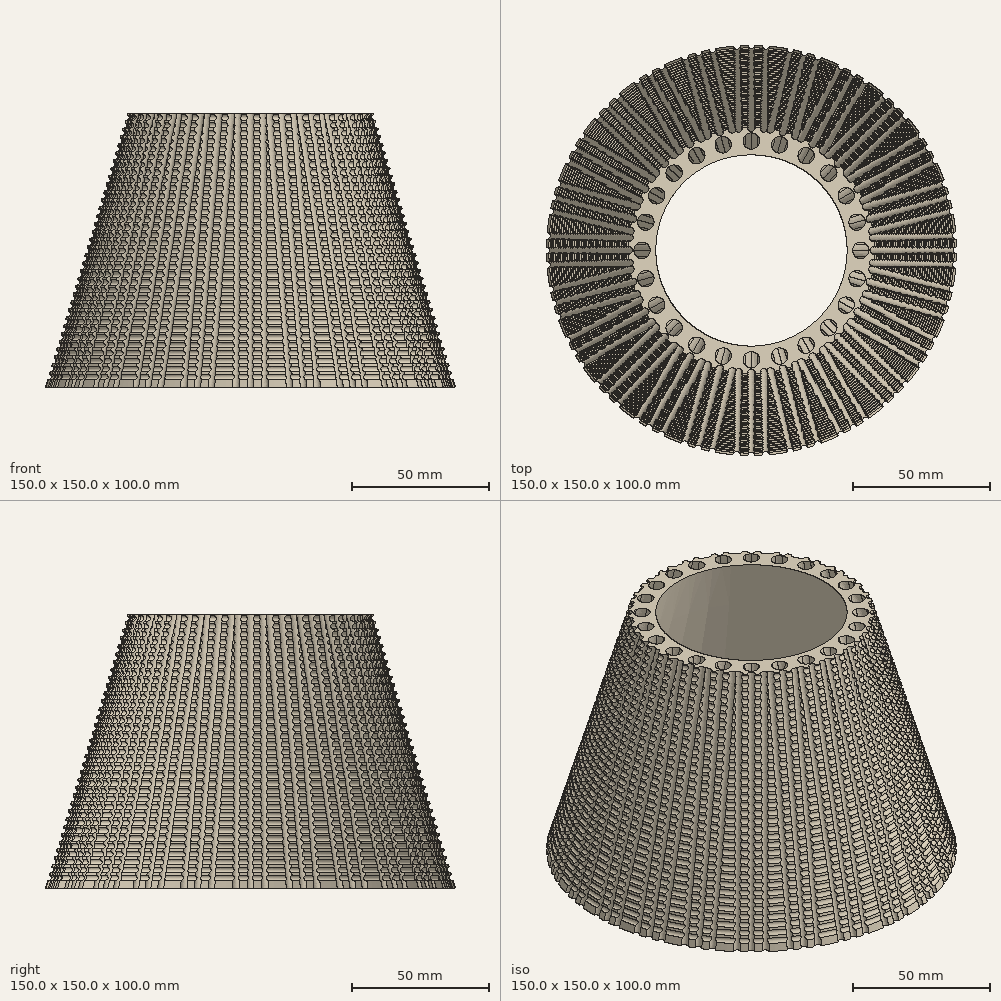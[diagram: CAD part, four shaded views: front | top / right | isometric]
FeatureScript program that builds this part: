
annotation { "Feature Type Name" : "Feature", "Feature Type Description" : "" }
export const myFeature = defineFeature(function(context is Context, id is Id, definition is map)
    precondition{}
    {
        {
            var Q0;
            Q0=qCreatedBy(makeId("Top.planeOp"),FACE);
            var sketch = newSketch(context, id + "F0", { "sketchPlane" : qUnion([Q0])});
            skCircle(sketch, "E0", {"center": v(0, 0) * mm, "radius": 75 * mm, "construction": true});
            skCircle(sketch, "E1", {"center": v(0, 0) * mm, "radius": 65 * mm, "construction": true});
            skLineSegment(sketch, "E2", {"start": v(-65, 0) * mm, "end": v(-75, 0) * mm, "construction": true});
            skCircle(sketch, "E3", {"center": v(-70, 0) * mm, "radius": 1 * mm});
            skCircle(sketch, "E4", {"center": v(-75, 0) * mm, "radius": 1.25 * mm});
            skLineSegment(sketch, "E5", {"start": v(0, 0) * mm, "end": v(-74.95, 2.62) * mm, "construction": true});
            skCircle(sketch, "E6", {"center": v(0, 0) * mm, "radius": 67.5 * mm, "construction": true});
            skCircle(sketch, "E7", {"center": v(0, 0) * mm, "radius": 72.5 * mm, "construction": true});
            skCircle(sketch, "E8", {"center": v(-72.46, 2.53) * mm, "radius": 1 * mm});
            skCircle(sketch, "E9", {"center": v(-67.46, 2.36) * mm, "radius": 1 * mm});
            skCircle(sketch, "E10", {"center": v(0, 0) * mm, "radius": 70 * mm, "construction": true});
            skLineSegment(sketch, "E11", {"start": v(0, 0) * mm, "end": v(-74.95, -2.62) * mm, "construction": true});
            skCircle(sketch, "E12", {"center": v(-67.46, -2.36) * mm, "radius": 1 * mm});
            skCircle(sketch, "E13", {"center": v(-72.46, -2.53) * mm, "radius": 1 * mm});
            skLineSegment(sketch, "E14", {"start": v(0, 0) * mm, "end": v(-74.82, -5.23) * mm, "construction": true});
            skLineSegment(sketch, "E15", {"start": v(0, 0) * mm, "end": v(-74.82, 5.23) * mm, "construction": true});
            skCircle(sketch, "E16", {"center": v(-74.82, -5.23) * mm, "radius": 1.25 * mm});
            skCircle(sketch, "E17", {"center": v(-74.82, 5.23) * mm, "radius": 1.25 * mm});
            skCircle(sketch, "E18", {"center": v(-69.83, -4.88) * mm, "radius": 1 * mm});
            skCircle(sketch, "E19", {"center": v(-69.83, 4.88) * mm, "radius": 1 * mm});
            skSolve(sketch);
        }
        {
            var Q0;
            Q0=qCreatedBy(makeId("Top.planeOp"),FACE);
            var sketch = newSketch(context, id + "F1", { "sketchPlane" : qUnion([Q0])});
            skCircle(sketch, "E20.0", {"center": v(0, 0) * mm, "radius": 75 * mm});
            skSolve(sketch);
        }
        {
            var Q0;
            Q0=qCreatedBy(makeId("Top.planeOp"),FACE);
            var sketch = newSketch(context, id + "F2", { "sketchPlane" : qUnion([Q0])});
            skCircle(sketch, "E21.0", {"center": v(0, 0) * mm, "radius": 65 * mm});
            skSolve(sketch);
        }
        {
            var Q0;
            Q0=qCreatedBy(makeId("Top.planeOp"),FACE);
            cPlane(context, id + "F3", {"entities" : qUnion([Q0]), "cplaneType" : CPlaneType.OFFSET, "offset" : 100 * mm, "width" : 150 * mm, "height" : 150 * mm});
        }
        {
            var Q0;
            Q0=qCreatedBy(id+"F3.planeOp",FACE);
            var sketch = newSketch(context, id + "F4", { "sketchPlane" : qUnion([Q0])});
            skCircle(sketch, "E22", {"center": v(0, 0) * mm, "radius": 35 * mm, "construction": true});
            skCircle(sketch, "E23", {"center": v(0, 0) * mm, "radius": 45 * mm, "construction": true});
            skLineSegment(sketch, "E24", {"start": v(-35, 0) * mm, "end": v(-45, 0) * mm, "construction": true});
            skCircle(sketch, "E25", {"center": v(0, 0) * mm, "radius": 37.5 * mm, "construction": true});
            skCircle(sketch, "E26", {"center": v(0, 0) * mm, "radius": 42.5 * mm, "construction": true});
            skCircle(sketch, "E27", {"center": v(-40, 0) * mm, "radius": 3 * mm});
            skCircle(sketch, "E28", {"center": v(-45, 0) * mm, "radius": 1.5 * mm});
            skLineSegment(sketch, "E29", {"start": v(0, 0) * mm, "end": v(-44.75, -4.7) * mm, "construction": true});
            skLineSegment(sketch, "E30", {"start": v(0, 0) * mm, "end": v(-44.75, 4.7) * mm, "construction": true});
            skCircle(sketch, "E31", {"center": v(-44.75, -4.7) * mm, "radius": 1.5 * mm});
            skCircle(sketch, "E32", {"center": v(-44.75, 4.7) * mm, "radius": 1.5 * mm});
            skSolve(sketch);
        }
        {
            var Q0;
            Q0=qCreatedBy(id+"F3.planeOp",FACE);
            var sketch = newSketch(context, id + "F5", { "sketchPlane" : qUnion([Q0])});
            skCircle(sketch, "E33.0", {"center": v(0, 0) * mm, "radius": 35 * mm});
            skSolve(sketch);
        }
        {
            var Q0;
            Q0=qCreatedBy(id+"F3.planeOp",FACE);
            var sketch = newSketch(context, id + "F6", { "sketchPlane" : qUnion([Q0])});
            skCircle(sketch, "E34.0", {"center": v(0, 0) * mm, "radius": 45 * mm});
            skSolve(sketch);
        }
        {
            var Q0;
            Q0=makeQuery(id+"F4.imprint","IMPRINT",FACE,{"disambiguationData":[TD([[makeQuery(id+"F4.imprint","IMPRINT",EDGE,{"derivedFrom":sQuery(id+"F4.wireOp",EDGE,"E28")}),1.0]])]});
            var Q1;
            Q1=makeQuery(id+"F0.imprint","IMPRINT",FACE,{"disambiguationData":[TD([[makeQuery(id+"F0.imprint","IMPRINT",EDGE,{"derivedFrom":sQuery(id+"F0.wireOp",EDGE,"E4")}),1.0]])]});
            loft(context, id + "F7", {"sheetProfilesArray" : [{ "sheetProfileEntities" : qUnion([Q0]) }, { "sheetProfileEntities" : qUnion([Q1]) }]});
        }
        {
            var Q1;
            Q1=makeQuery(id+"F4.imprint","IMPRINT",FACE,{"disambiguationData":[TD([[makeQuery(id+"F4.imprint","IMPRINT",EDGE,{"derivedFrom":sQuery(id+"F4.wireOp",EDGE,"E27")}),1.0]])]});
            var Q2;
            Q2=makeQuery(id+"F0.imprint","IMPRINT",FACE,{"disambiguationData":[TD([[makeQuery(id+"F0.imprint","IMPRINT",EDGE,{"derivedFrom":sQuery(id+"F0.wireOp",EDGE,"E8")}),1.0]])]});
            loft(context, id + "F8", {"operationType" : NewBodyOperationType.ADD, "sheetProfilesArray" : [{ "sheetProfileEntities" : qUnion([Q1]) }, { "sheetProfileEntities" : qUnion([Q2]) }]});
        }
        {
            var Q1;
            Q1=makeQuery(id+"F4.imprint","IMPRINT",FACE,{"disambiguationData":[TD([[makeQuery(id+"F4.imprint","IMPRINT",EDGE,{"derivedFrom":sQuery(id+"F4.wireOp",EDGE,"E27")}),1.0]])]});
            var Q2;
            Q2=makeQuery(id+"F0.imprint","IMPRINT",FACE,{"disambiguationData":[TD([[makeQuery(id+"F0.imprint","IMPRINT",EDGE,{"derivedFrom":sQuery(id+"F0.wireOp",EDGE,"E9")}),1.0]])]});
            loft(context, id + "F9", {"operationType" : NewBodyOperationType.ADD, "sheetProfilesArray" : [{ "sheetProfileEntities" : qUnion([Q1]) }, { "sheetProfileEntities" : qUnion([Q2]) }]});
        }
        {
            var Q1;
            Q1=makeQuery(id+"F4.imprint","IMPRINT",FACE,{"disambiguationData":[TD([[makeQuery(id+"F4.imprint","IMPRINT",EDGE,{"derivedFrom":sQuery(id+"F4.wireOp",EDGE,"E27")}),1.0]])]});
            var Q2;
            Q2=makeQuery(id+"F0.imprint","IMPRINT",FACE,{"disambiguationData":[TD([[makeQuery(id+"F0.imprint","IMPRINT",EDGE,{"derivedFrom":sQuery(id+"F0.wireOp",EDGE,"E19")}),1.0]])]});
            loft(context, id + "F10", {"operationType" : NewBodyOperationType.ADD, "sheetProfilesArray" : [{ "sheetProfileEntities" : qUnion([Q1]) }, { "sheetProfileEntities" : qUnion([Q2]) }]});
        }
        {
            var Q1;
            Q1=makeQuery(id+"F4.imprint","IMPRINT",FACE,{"disambiguationData":[TD([[makeQuery(id+"F4.imprint","IMPRINT",EDGE,{"derivedFrom":sQuery(id+"F4.wireOp",EDGE,"E27")}),1.0]])]});
            var Q2;
            Q2=makeQuery(id+"F0.imprint","IMPRINT",FACE,{"disambiguationData":[TD([[makeQuery(id+"F0.imprint","IMPRINT",EDGE,{"derivedFrom":sQuery(id+"F0.wireOp",EDGE,"E3")}),1.0]])]});
            loft(context, id + "F11", {"operationType" : NewBodyOperationType.ADD, "sheetProfilesArray" : [{ "sheetProfileEntities" : qUnion([Q1]) }, { "sheetProfileEntities" : qUnion([Q2]) }]});
        }
        {
            var Q1;
            Q1=makeQuery(id+"F4.imprint","IMPRINT",FACE,{"disambiguationData":[TD([[makeQuery(id+"F4.imprint","IMPRINT",EDGE,{"derivedFrom":sQuery(id+"F4.wireOp",EDGE,"E27")}),1.0]])]});
            var Q2;
            Q2=makeQuery(id+"F0.imprint","IMPRINT",FACE,{"disambiguationData":[TD([[makeQuery(id+"F0.imprint","IMPRINT",EDGE,{"derivedFrom":sQuery(id+"F0.wireOp",EDGE,"E12")}),1.0]])]});
            loft(context, id + "F12", {"operationType" : NewBodyOperationType.ADD, "sheetProfilesArray" : [{ "sheetProfileEntities" : qUnion([Q1]) }, { "sheetProfileEntities" : qUnion([Q2]) }]});
        }
        {
            var Q1;
            Q1=makeQuery(id+"F4.imprint","IMPRINT",FACE,{"disambiguationData":[TD([[makeQuery(id+"F4.imprint","IMPRINT",EDGE,{"derivedFrom":sQuery(id+"F4.wireOp",EDGE,"E27")}),1.0]])]});
            var Q2;
            Q2=makeQuery(id+"F0.imprint","IMPRINT",FACE,{"disambiguationData":[TD([[makeQuery(id+"F0.imprint","IMPRINT",EDGE,{"derivedFrom":sQuery(id+"F0.wireOp",EDGE,"E13")}),1.0]])]});
            loft(context, id + "F13", {"operationType" : NewBodyOperationType.ADD, "sheetProfilesArray" : [{ "sheetProfileEntities" : qUnion([Q1]) }, { "sheetProfileEntities" : qUnion([Q2]) }]});
        }
        {
            var Q1;
            Q1=makeQuery(id+"F4.imprint","IMPRINT",FACE,{"disambiguationData":[TD([[makeQuery(id+"F4.imprint","IMPRINT",EDGE,{"derivedFrom":sQuery(id+"F4.wireOp",EDGE,"E27")}),1.0]])]});
            var Q2;
            Q2=makeQuery(id+"F0.imprint","IMPRINT",FACE,{"disambiguationData":[TD([[makeQuery(id+"F0.imprint","IMPRINT",EDGE,{"derivedFrom":sQuery(id+"F0.wireOp",EDGE,"E18")}),1.0]])]});
            loft(context, id + "F14", {"operationType" : NewBodyOperationType.ADD, "sheetProfilesArray" : [{ "sheetProfileEntities" : qUnion([Q1]) }, { "sheetProfileEntities" : qUnion([Q2]) }]});
        }
        {
            var Q0;
            Q0=makeQuery(id+"F4.imprint","IMPRINT",FACE,{"disambiguationData":[TD([[makeQuery(id+"F4.imprint","IMPRINT",EDGE,{"derivedFrom":sQuery(id+"F4.wireOp",EDGE,"E32")}),1.0]])]});
            var Q1;
            Q1=makeQuery(id+"F0.imprint","IMPRINT",FACE,{"disambiguationData":[TD([[makeQuery(id+"F0.imprint","IMPRINT",EDGE,{"derivedFrom":sQuery(id+"F0.wireOp",EDGE,"E17")}),1.0]])]});
            loft(context, id + "F15", {"sheetProfilesArray" : [{ "sheetProfileEntities" : qUnion([Q0]) }, { "sheetProfileEntities" : qUnion([Q1]) }]});
        }
        {
            var Q0;
            Q0=makeQuery(id+"F4.imprint","IMPRINT",FACE,{"disambiguationData":[TD([[makeQuery(id+"F4.imprint","IMPRINT",EDGE,{"derivedFrom":sQuery(id+"F4.wireOp",EDGE,"E31")}),1.0]])]});
            var Q1;
            Q1=makeQuery(id+"F0.imprint","IMPRINT",FACE,{"disambiguationData":[TD([[makeQuery(id+"F0.imprint","IMPRINT",EDGE,{"derivedFrom":sQuery(id+"F0.wireOp",EDGE,"E16")}),1.0]])]});
            loft(context, id + "F16", {"sheetProfilesArray" : [{ "sheetProfileEntities" : qUnion([Q0]) }, { "sheetProfileEntities" : qUnion([Q1]) }]});
        }
        {
            var Q0;
            Q0=makeQuery(id+"F1.imprint","IMPRINT",FACE,{"disambiguationData":[TD([[makeQuery(id+"F1.imprint","IMPRINT",EDGE,{"derivedFrom":sQuery(id+"F1.wireOp",EDGE,"E20.0")}),1.0]])]});
            var Q1;
            Q1=makeQuery(id+"F6.imprint","IMPRINT",FACE,{"disambiguationData":[TD([[makeQuery(id+"F6.imprint","IMPRINT",EDGE,{"derivedFrom":sQuery(id+"F6.wireOp",EDGE,"E34.0")}),1.0]])]});
            loft(context, id + "F17", {"sheetProfilesArray" : [{ "sheetProfileEntities" : qUnion([Q0]) }, { "sheetProfileEntities" : qUnion([Q1]) }]});
        }
        {
            var Q1;
            Q1=makeQuery(id+"F2.imprint","IMPRINT",FACE,{"disambiguationData":[TD([[makeQuery(id+"F2.imprint","IMPRINT",EDGE,{"derivedFrom":sQuery(id+"F2.wireOp",EDGE,"E21.0")}),1.0]])]});
            var Q2;
            Q2=makeQuery(id+"F5.imprint","IMPRINT",FACE,{"disambiguationData":[TD([[makeQuery(id+"F5.imprint","IMPRINT",EDGE,{"derivedFrom":sQuery(id+"F5.wireOp",EDGE,"E33.0")}),1.0]])]});
            loft(context, id + "F18", {"operationType" : NewBodyOperationType.REMOVE, "sheetProfilesArray" : [{ "sheetProfileEntities" : qUnion([Q1]) }, { "sheetProfileEntities" : qUnion([Q2]) }]});
        }
        {
            var Q0;
            Q0=makeQuery(id+"F7.opLoft","SWEPT_BODY",BODY,{"disambiguationData":[OSD([makeQuery(id+"F0.imprint","IMPRINT",FACE,{"disambiguationData":[TD([[makeQuery(id+"F0.imprint","IMPRINT",EDGE,{"derivedFrom":sQuery(id+"F0.wireOp",EDGE,"E4")}),1.0]])]}),makeQuery(id+"F4.imprint","IMPRINT",FACE,{"disambiguationData":[TD([[makeQuery(id+"F4.imprint","IMPRINT",EDGE,{"derivedFrom":sQuery(id+"F4.wireOp",EDGE,"E28")}),1.0]])]})])]});
            var Q1;
            Q1=makeQuery(id+"F8.opLoft","SWEPT_BODY",BODY,{"disambiguationData":[OSD([makeQuery(id+"F0.imprint","IMPRINT",FACE,{"disambiguationData":[TD([[makeQuery(id+"F0.imprint","IMPRINT",EDGE,{"derivedFrom":sQuery(id+"F0.wireOp",EDGE,"E8")}),1.0]])]}),makeQuery(id+"F4.imprint","IMPRINT",FACE,{"disambiguationData":[TD([[makeQuery(id+"F4.imprint","IMPRINT",EDGE,{"derivedFrom":sQuery(id+"F4.wireOp",EDGE,"E27")}),1.0]])]})])]});
            var Q2;
            Q2=makeQuery(id+"F15.opLoft","SWEPT_BODY",BODY,{"disambiguationData":[OSD([makeQuery(id+"F0.imprint","IMPRINT",FACE,{"disambiguationData":[TD([[makeQuery(id+"F0.imprint","IMPRINT",EDGE,{"derivedFrom":sQuery(id+"F0.wireOp",EDGE,"E17")}),1.0]])]}),makeQuery(id+"F4.imprint","IMPRINT",FACE,{"disambiguationData":[TD([[makeQuery(id+"F4.imprint","IMPRINT",EDGE,{"derivedFrom":sQuery(id+"F4.wireOp",EDGE,"E32")}),1.0]])]})])]});
            var Q3;
            Q3=makeQuery(id+"F16.opLoft","SWEPT_BODY",BODY,{"disambiguationData":[OSD([makeQuery(id+"F0.imprint","IMPRINT",FACE,{"disambiguationData":[TD([[makeQuery(id+"F0.imprint","IMPRINT",EDGE,{"derivedFrom":sQuery(id+"F0.wireOp",EDGE,"E16")}),1.0]])]}),makeQuery(id+"F4.imprint","IMPRINT",FACE,{"disambiguationData":[TD([[makeQuery(id+"F4.imprint","IMPRINT",EDGE,{"derivedFrom":sQuery(id+"F4.wireOp",EDGE,"E31")}),1.0]])]})])]});
            var Q4;
            Q4=sQuery(id+"F5.wireOp",EDGE,"E33.0");
            circularPattern(context, id + "F19", {"operationType" : NewBodyOperationType.REMOVE, "entities" : qUnion([Q0, Q1, Q2, Q3]), "axis" : qUnion([Q4]), "angle" : 15 * degree, "instanceCount" : 24});
        }
        {
            var Q0;
            Q0=qCreatedBy(makeId("Front.planeOp"),FACE);
            var sketch = newSketch(context, id + "F20", { "sketchPlane" : qUnion([Q0])});
            skFitSpline(sketch, "E35.0", {"points": [v(-74.99, 0) * mm, v(-64.99, 33.33) * mm, v(-54.98, 66.67) * mm, v(-44.98, 100) * mm], "construction": true});
            skCircle(sketch, "E36", {"center": v(-73.84, 3.83) * mm, "radius": 1 * mm});
            skLineSegment(sketch, "E37", {"start": v(0, 0) * mm, "end": v(0, 84.84) * mm});
            skCircle(sketch, "E38.1.0.0", {"center": v(-72.98, 6.7) * mm, "radius": 1 * mm});
            skCircle(sketch, "E38.2.0.0", {"center": v(-72.12, 9.58) * mm, "radius": 1 * mm});
            skLineSegment(sketch, "E38.direction1", {"start": v(-73.84, 3.83) * mm, "end": v(-72.98, 6.7) * mm, "construction": true});
            skCircle(sketch, "E39.0.3.0", {"center": v(-71.25, 12.45) * mm, "radius": 1 * mm});
            skCircle(sketch, "E39.0.4.0", {"center": v(-70.4, 15.32) * mm, "radius": 1 * mm});
            skCircle(sketch, "E39.0.5.0", {"center": v(-69.53, 18.2) * mm, "radius": 1 * mm});
            skCircle(sketch, "E39.0.6.0", {"center": v(-68.67, 21.07) * mm, "radius": 1 * mm});
            skCircle(sketch, "E39.0.7.0", {"center": v(-67.8, 23.95) * mm, "radius": 1 * mm});
            skCircle(sketch, "E39.0.8.0", {"center": v(-66.94, 26.82) * mm, "radius": 1 * mm});
            skCircle(sketch, "E39.0.9.0", {"center": v(-66.08, 29.7) * mm, "radius": 1 * mm});
            skCircle(sketch, "E39.0.10.0", {"center": v(-65.22, 32.57) * mm, "radius": 1 * mm});
            skCircle(sketch, "E39.0.11.0", {"center": v(-64.35, 35.44) * mm, "radius": 1 * mm});
            skCircle(sketch, "E39.0.12.0", {"center": v(-63.5, 38.31) * mm, "radius": 1 * mm});
            skCircle(sketch, "E39.0.13.0", {"center": v(-62.63, 41.19) * mm, "radius": 1 * mm});
            skCircle(sketch, "E39.0.14.0", {"center": v(-61.77, 44.06) * mm, "radius": 1 * mm});
            skCircle(sketch, "E39.0.15.0", {"center": v(-60.9, 46.93) * mm, "radius": 1 * mm});
            skCircle(sketch, "E39.0.16.0", {"center": v(-60.04, 49.8) * mm, "radius": 1 * mm});
            skCircle(sketch, "E39.0.17.0", {"center": v(-59.18, 52.68) * mm, "radius": 1 * mm});
            skCircle(sketch, "E39.0.18.0", {"center": v(-58.32, 55.55) * mm, "radius": 1 * mm});
            skCircle(sketch, "E39.0.19.0", {"center": v(-57.46, 58.43) * mm, "radius": 1 * mm});
            skCircle(sketch, "E40.0.20.0", {"center": v(-56.6, 61.3) * mm, "radius": 1 * mm});
            skCircle(sketch, "E40.0.21.0", {"center": v(-55.73, 64.17) * mm, "radius": 1 * mm});
            skCircle(sketch, "E40.0.22.0", {"center": v(-54.87, 67.05) * mm, "radius": 1 * mm});
            skCircle(sketch, "E40.0.23.0", {"center": v(-54, 69.92) * mm, "radius": 1 * mm});
            skCircle(sketch, "E40.0.24.0", {"center": v(-53.15, 72.8) * mm, "radius": 1 * mm});
            skCircle(sketch, "E40.0.25.0", {"center": v(-52.28, 75.67) * mm, "radius": 1 * mm});
            skCircle(sketch, "E40.0.26.0", {"center": v(-51.42, 78.54) * mm, "radius": 1 * mm});
            skCircle(sketch, "E40.0.27.0", {"center": v(-50.56, 81.41) * mm, "radius": 1 * mm});
            skCircle(sketch, "E40.0.28.0", {"center": v(-49.7, 84.29) * mm, "radius": 1 * mm});
            skCircle(sketch, "E40.0.29.0", {"center": v(-48.83, 87.16) * mm, "radius": 1 * mm});
            skCircle(sketch, "E40.0.30.0", {"center": v(-47.97, 90.03) * mm, "radius": 1 * mm});
            skCircle(sketch, "E40.0.31.0", {"center": v(-47.1, 92.9) * mm, "radius": 1 * mm});
            skCircle(sketch, "E40.0.32.0", {"center": v(-46.25, 95.78) * mm, "radius": 1 * mm});
            skCircle(sketch, "E40.0.33.0", {"center": v(-45.38, 98.65) * mm, "radius": 1 * mm});
            skSolve(sketch);
        }
        {
            var Q0;
            Q0=makeQuery(id+"F20.imprint","IMPRINT",FACE,{"disambiguationData":[TD([[makeQuery(id+"F20.imprint","IMPRINT",EDGE,{"derivedFrom":sQuery(id+"F20.wireOp",EDGE,"E36")}),1.0]])]});
            var Q1;
            Q1=makeQuery(id+"F20.imprint","IMPRINT",FACE,{"disambiguationData":[TD([[makeQuery(id+"F20.imprint","IMPRINT",EDGE,{"derivedFrom":sQuery(id+"F20.wireOp",EDGE,"E38.1.0.0")}),1.0]])]});
            var Q2;
            Q2=makeQuery(id+"F20.imprint","IMPRINT",FACE,{"disambiguationData":[TD([[makeQuery(id+"F20.imprint","IMPRINT",EDGE,{"derivedFrom":sQuery(id+"F20.wireOp",EDGE,"E38.2.0.0")}),1.0]])]});
            var Q3;
            Q3=makeQuery(id+"F20.imprint","IMPRINT",FACE,{"disambiguationData":[TD([[makeQuery(id+"F20.imprint","IMPRINT",EDGE,{"derivedFrom":sQuery(id+"F20.wireOp",EDGE,"E39.0.3.0")}),1.0]])]});
            var Q4;
            Q4=makeQuery(id+"F20.imprint","IMPRINT",FACE,{"disambiguationData":[TD([[makeQuery(id+"F20.imprint","IMPRINT",EDGE,{"derivedFrom":sQuery(id+"F20.wireOp",EDGE,"E39.0.4.0")}),1.0]])]});
            var Q5;
            Q5=makeQuery(id+"F20.imprint","IMPRINT",FACE,{"disambiguationData":[TD([[makeQuery(id+"F20.imprint","IMPRINT",EDGE,{"derivedFrom":sQuery(id+"F20.wireOp",EDGE,"E39.0.5.0")}),1.0]])]});
            var Q6;
            Q6=makeQuery(id+"F20.imprint","IMPRINT",FACE,{"disambiguationData":[TD([[makeQuery(id+"F20.imprint","IMPRINT",EDGE,{"derivedFrom":sQuery(id+"F20.wireOp",EDGE,"E39.0.6.0")}),1.0]])]});
            var Q7;
            Q7=makeQuery(id+"F20.imprint","IMPRINT",FACE,{"disambiguationData":[TD([[makeQuery(id+"F20.imprint","IMPRINT",EDGE,{"derivedFrom":sQuery(id+"F20.wireOp",EDGE,"E39.0.7.0")}),1.0]])]});
            var Q8;
            Q8=makeQuery(id+"F20.imprint","IMPRINT",FACE,{"disambiguationData":[TD([[makeQuery(id+"F20.imprint","IMPRINT",EDGE,{"derivedFrom":sQuery(id+"F20.wireOp",EDGE,"E39.0.8.0")}),1.0]])]});
            var Q9;
            Q9=makeQuery(id+"F20.imprint","IMPRINT",FACE,{"disambiguationData":[TD([[makeQuery(id+"F20.imprint","IMPRINT",EDGE,{"derivedFrom":sQuery(id+"F20.wireOp",EDGE,"E39.0.9.0")}),1.0]])]});
            var Q10;
            Q10=makeQuery(id+"F20.imprint","IMPRINT",FACE,{"disambiguationData":[TD([[makeQuery(id+"F20.imprint","IMPRINT",EDGE,{"derivedFrom":sQuery(id+"F20.wireOp",EDGE,"E39.0.10.0")}),1.0]])]});
            var Q11;
            Q11=makeQuery(id+"F20.imprint","IMPRINT",FACE,{"disambiguationData":[TD([[makeQuery(id+"F20.imprint","IMPRINT",EDGE,{"derivedFrom":sQuery(id+"F20.wireOp",EDGE,"E39.0.11.0")}),1.0]])]});
            var Q12;
            Q12=makeQuery(id+"F20.imprint","IMPRINT",FACE,{"disambiguationData":[TD([[makeQuery(id+"F20.imprint","IMPRINT",EDGE,{"derivedFrom":sQuery(id+"F20.wireOp",EDGE,"E39.0.12.0")}),1.0]])]});
            var Q13;
            Q13=makeQuery(id+"F20.imprint","IMPRINT",FACE,{"disambiguationData":[TD([[makeQuery(id+"F20.imprint","IMPRINT",EDGE,{"derivedFrom":sQuery(id+"F20.wireOp",EDGE,"E39.0.13.0")}),1.0]])]});
            var Q14;
            Q14=makeQuery(id+"F20.imprint","IMPRINT",FACE,{"disambiguationData":[TD([[makeQuery(id+"F20.imprint","IMPRINT",EDGE,{"derivedFrom":sQuery(id+"F20.wireOp",EDGE,"E39.0.14.0")}),1.0]])]});
            var Q15;
            Q15=makeQuery(id+"F20.imprint","IMPRINT",FACE,{"disambiguationData":[TD([[makeQuery(id+"F20.imprint","IMPRINT",EDGE,{"derivedFrom":sQuery(id+"F20.wireOp",EDGE,"E39.0.15.0")}),1.0]])]});
            var Q16;
            Q16=makeQuery(id+"F20.imprint","IMPRINT",FACE,{"disambiguationData":[TD([[makeQuery(id+"F20.imprint","IMPRINT",EDGE,{"derivedFrom":sQuery(id+"F20.wireOp",EDGE,"E39.0.16.0")}),1.0]])]});
            var Q17;
            Q17=makeQuery(id+"F20.imprint","IMPRINT",FACE,{"disambiguationData":[TD([[makeQuery(id+"F20.imprint","IMPRINT",EDGE,{"derivedFrom":sQuery(id+"F20.wireOp",EDGE,"E39.0.17.0")}),1.0]])]});
            var Q18;
            Q18=makeQuery(id+"F20.imprint","IMPRINT",FACE,{"disambiguationData":[TD([[makeQuery(id+"F20.imprint","IMPRINT",EDGE,{"derivedFrom":sQuery(id+"F20.wireOp",EDGE,"E39.0.18.0")}),1.0]])]});
            var Q19;
            Q19=makeQuery(id+"F20.imprint","IMPRINT",FACE,{"disambiguationData":[TD([[makeQuery(id+"F20.imprint","IMPRINT",EDGE,{"derivedFrom":sQuery(id+"F20.wireOp",EDGE,"E39.0.19.0")}),1.0]])]});
            var Q20;
            Q20=makeQuery(id+"F20.imprint","IMPRINT",FACE,{"disambiguationData":[TD([[makeQuery(id+"F20.imprint","IMPRINT",EDGE,{"derivedFrom":sQuery(id+"F20.wireOp",EDGE,"E40.0.20.0")}),1.0]])]});
            var Q21;
            Q21=makeQuery(id+"F20.imprint","IMPRINT",FACE,{"disambiguationData":[TD([[makeQuery(id+"F20.imprint","IMPRINT",EDGE,{"derivedFrom":sQuery(id+"F20.wireOp",EDGE,"E40.0.21.0")}),1.0]])]});
            var Q22;
            Q22=makeQuery(id+"F20.imprint","IMPRINT",FACE,{"disambiguationData":[TD([[makeQuery(id+"F20.imprint","IMPRINT",EDGE,{"derivedFrom":sQuery(id+"F20.wireOp",EDGE,"E40.0.22.0")}),1.0]])]});
            var Q23;
            Q23=makeQuery(id+"F20.imprint","IMPRINT",FACE,{"disambiguationData":[TD([[makeQuery(id+"F20.imprint","IMPRINT",EDGE,{"derivedFrom":sQuery(id+"F20.wireOp",EDGE,"E40.0.23.0")}),1.0]])]});
            var Q24;
            Q24=makeQuery(id+"F20.imprint","IMPRINT",FACE,{"disambiguationData":[TD([[makeQuery(id+"F20.imprint","IMPRINT",EDGE,{"derivedFrom":sQuery(id+"F20.wireOp",EDGE,"E40.0.24.0")}),1.0]])]});
            var Q25;
            Q25=makeQuery(id+"F20.imprint","IMPRINT",FACE,{"disambiguationData":[TD([[makeQuery(id+"F20.imprint","IMPRINT",EDGE,{"derivedFrom":sQuery(id+"F20.wireOp",EDGE,"E40.0.25.0")}),1.0]])]});
            var Q26;
            Q26=makeQuery(id+"F20.imprint","IMPRINT",FACE,{"disambiguationData":[TD([[makeQuery(id+"F20.imprint","IMPRINT",EDGE,{"derivedFrom":sQuery(id+"F20.wireOp",EDGE,"E40.0.26.0")}),1.0]])]});
            var Q27;
            Q27=makeQuery(id+"F20.imprint","IMPRINT",FACE,{"disambiguationData":[TD([[makeQuery(id+"F20.imprint","IMPRINT",EDGE,{"derivedFrom":sQuery(id+"F20.wireOp",EDGE,"E40.0.27.0")}),1.0]])]});
            var Q28;
            Q28=makeQuery(id+"F20.imprint","IMPRINT",FACE,{"disambiguationData":[TD([[makeQuery(id+"F20.imprint","IMPRINT",EDGE,{"derivedFrom":sQuery(id+"F20.wireOp",EDGE,"E40.0.28.0")}),1.0]])]});
            var Q29;
            Q29=makeQuery(id+"F20.imprint","IMPRINT",FACE,{"disambiguationData":[TD([[makeQuery(id+"F20.imprint","IMPRINT",EDGE,{"derivedFrom":sQuery(id+"F20.wireOp",EDGE,"E40.0.29.0")}),1.0]])]});
            var Q30;
            Q30=makeQuery(id+"F20.imprint","IMPRINT",FACE,{"disambiguationData":[TD([[makeQuery(id+"F20.imprint","IMPRINT",EDGE,{"derivedFrom":sQuery(id+"F20.wireOp",EDGE,"E40.0.30.0")}),1.0]])]});
            var Q31;
            Q31=makeQuery(id+"F20.imprint","IMPRINT",FACE,{"disambiguationData":[TD([[makeQuery(id+"F20.imprint","IMPRINT",EDGE,{"derivedFrom":sQuery(id+"F20.wireOp",EDGE,"E40.0.31.0")}),1.0]])]});
            var Q32;
            Q32=makeQuery(id+"F20.imprint","IMPRINT",FACE,{"disambiguationData":[TD([[makeQuery(id+"F20.imprint","IMPRINT",EDGE,{"derivedFrom":sQuery(id+"F20.wireOp",EDGE,"E40.0.32.0")}),1.0]])]});
            var Q33;
            Q33=makeQuery(id+"F20.imprint","IMPRINT",FACE,{"disambiguationData":[TD([[makeQuery(id+"F20.imprint","IMPRINT",EDGE,{"derivedFrom":sQuery(id+"F20.wireOp",EDGE,"E40.0.33.0")}),1.0]])]});
            var Q34;
            Q34=sQuery(id+"F20.wireOp",EDGE,"E37");
            revolve(context, id + "F21", {"operationType" : NewBodyOperationType.REMOVE, "entities" : qUnion([Q0, Q1, Q2, Q3, Q4, Q5, Q6, Q7, Q8, Q9, Q10, Q11, Q12, Q13, Q14, Q15, Q16, Q17, Q18, Q19, Q20, Q21, Q22, Q23, Q24, Q25, Q26, Q27, Q28, Q29, Q30, Q31, Q32, Q33]), "axis" : qUnion([Q34]), "revolveType" : RevolveType.FULL, "oppositeDirection" : true});
        }
    });
